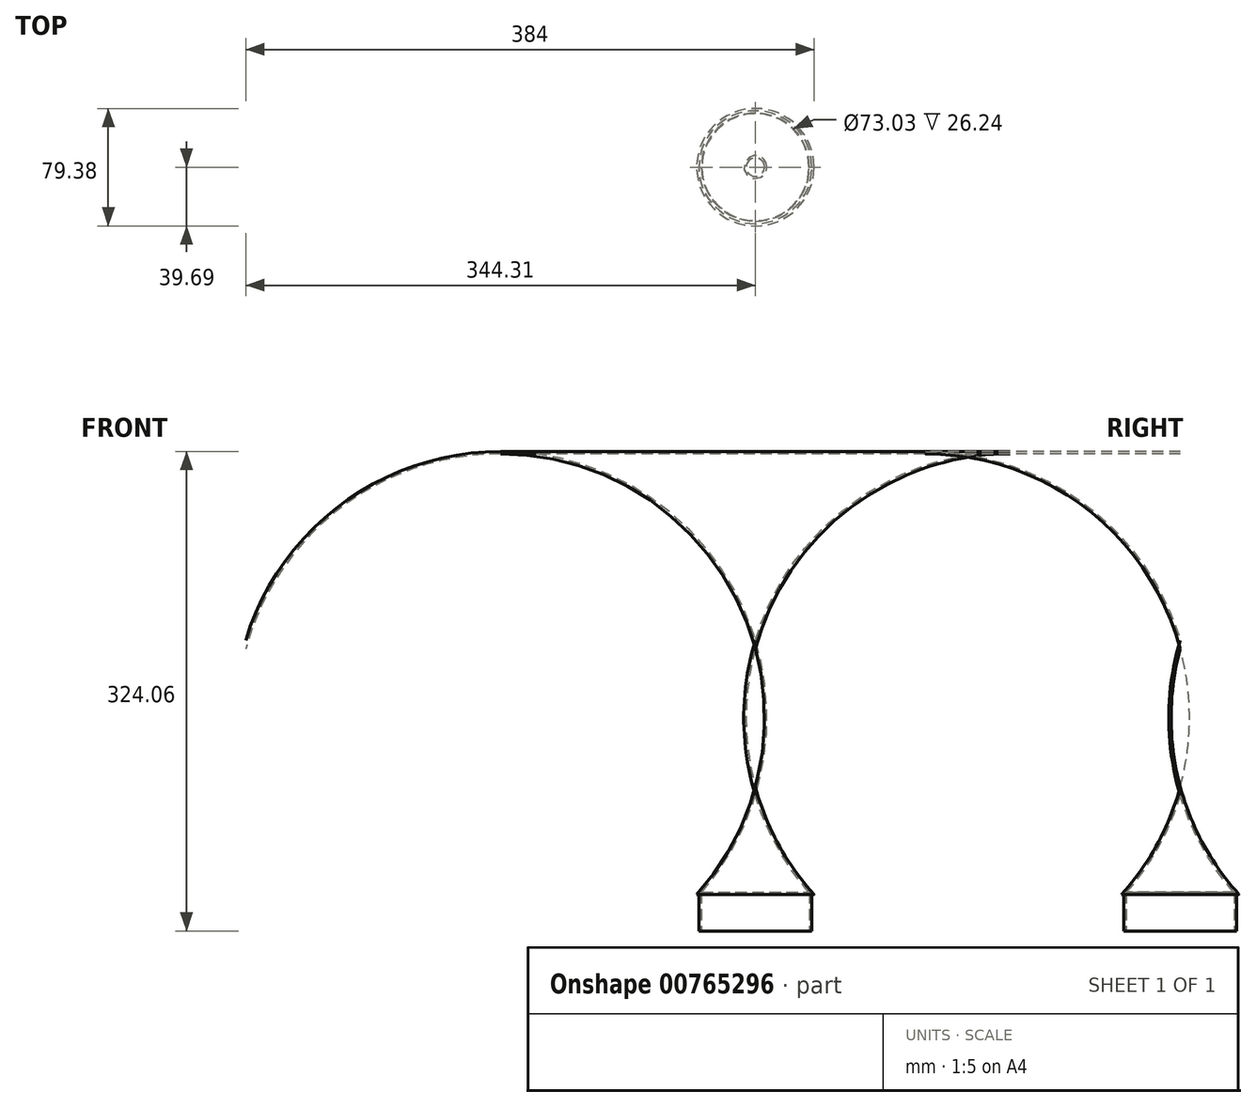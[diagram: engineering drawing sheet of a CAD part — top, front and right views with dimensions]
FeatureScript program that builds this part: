
annotation { "Feature Type Name" : "Feature", "Feature Type Description" : "" }
export const myFeature = defineFeature(function(context is Context, id is Id, definition is map)
    precondition{}
    {
        {
            var Q0;
            Q0=qCreatedBy(makeId("Front.planeOp"),FACE);
            var sketch = newSketch(context, id + "F0", { "sketchPlane" : qUnion([Q0])});
            skLineSegment(sketch, "E0", {"start": v(0, 0) * mm, "end": v(0, 91.69) * mm});
            skLineSegment(sketch, "E1", {"start": v(36.51, 0) * mm, "end": v(38.1, 0) * mm});
            skLineSegment(sketch, "E2", {"start": v(38.1, 0) * mm, "end": v(38.1, 24.65) * mm});
            skLineSegment(sketch, "E3", {"start": v(38.1, 24.65) * mm, "end": v(39.69, 24.65) * mm});
            skArc(sketch, "E4", {"start": v(0, 97.43) * mm, "mid": v(15.56, 58.7) * mm, "end": v(39.69, 24.65) * mm});
            skArc(sketch, "E5.0", {"start": v(0, 91.69) * mm, "mid": v(14.65, 57.06) * mm, "end": v(36.17, 26.24) * mm});
            skLineSegment(sketch, "E5.1", {"start": v(36.17, 26.24) * mm, "end": v(36.51, 26.24) * mm});
            skLineSegment(sketch, "E5.2", {"start": v(36.51, 0) * mm, "end": v(36.51, 26.24) * mm});
            skLineSegment(sketch, "E6", {"start": v(0, 97.43) * mm, "end": v(0, 91.69) * mm});
            skSolve(sketch);
        }
        {
            var Q0;
            Q0=makeQuery(id+"F0.imprint","IMPRINT",FACE,{"disambiguationData":[TD([[makeQuery(id+"F0.imprint","IMPRINT",EDGE,{"derivedFrom":sQuery(id+"F0.wireOp",EDGE,"E1")}),1.0]])]});
            var Q1;
            Q1=sQuery(id+"F0.wireOp",EDGE,"E0");
            revolve(context, id + "F1", {"surfaceOperationType" : NewSurfaceOperationType.NEW, "entities" : qUnion([Q0]), "axis" : qUnion([Q1]), "revolveType" : RevolveType.FULL});
        }
    });
